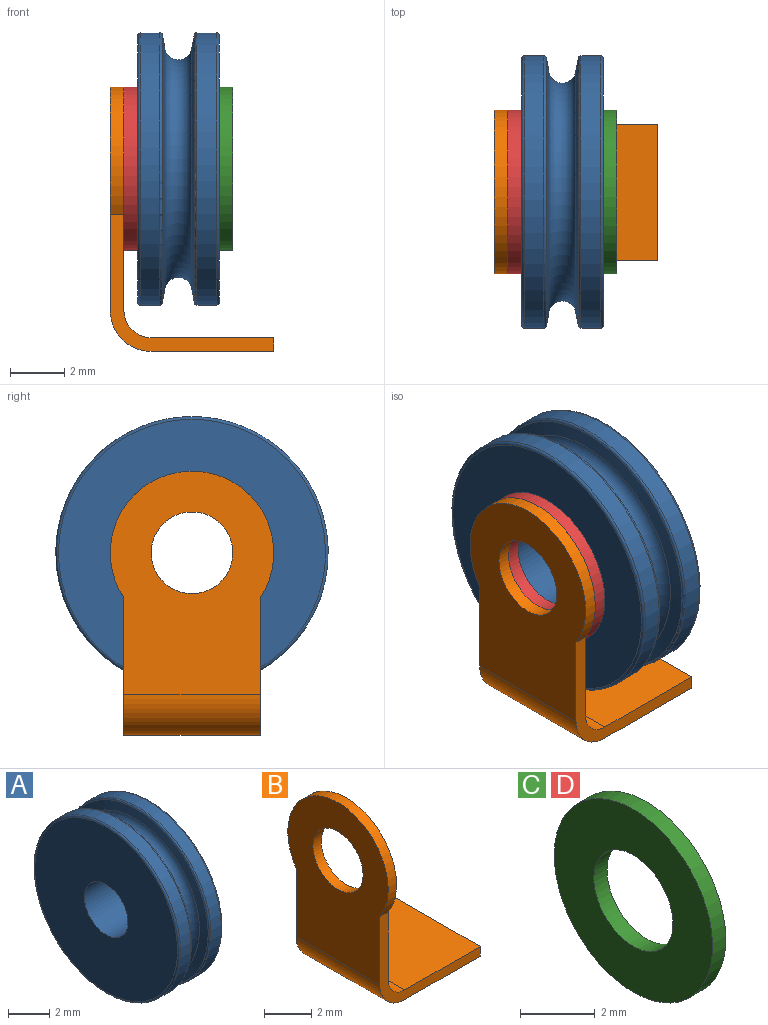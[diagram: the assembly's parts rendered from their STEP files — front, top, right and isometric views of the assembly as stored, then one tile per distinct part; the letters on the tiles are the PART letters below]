
ASSEMBLY  parts=4 mates=3
PART A: 12 faces, bbox 3x10.8x10.8 mm
  f0: cylinder r=1.5mm len=3mm, axis (-1,0,0), area 28.3mm2, adj f1,f2
  f1: plane 9.8x9.8mm, normal (1,0,0), area 68.4mm2, adj f0,f10
  f2: plane 9.8x9.8mm, normal (-1,0,0), area 68.4mm2, adj f0,f9
  f3: torus R=4.5mm, axis (-1,0,0), area 36.2mm2, adj f5,f6
  f4: cylinder r=5mm len=10mm, axis (-1,0,0), area 22.5mm2, adj f10,f11
  f5: cone r=5mm half-angle=79.6deg, axis (1,0,0), area 15.1mm2, adj f3,f11
  f6: cone r=5mm half-angle=79.6deg, axis (-1,0,0), area 15.1mm2, adj f3,f8
  f7: cylinder r=5mm len=10mm, axis (-1,0,0), area 22.5mm2, adj f8,f9
  f8: torus R=4.9mm, axis (1,0,0), area 4.3mm2, adj f6,f7
  f9: torus R=4.9mm, axis (1,0,0), area 4.9mm2, adj f2,f7
  f10: torus R=4.9mm, axis (1,0,0), area 4.9mm2, adj f1,f4
  f11: torus R=4.9mm, axis (1,0,0), area 4.3mm2, adj f4,f5
PART B: 11 faces, bbox 6x6x9.7 mm
  f0: plane 5x4.5mm, normal (0,0,-1), area 22.5mm2, adj f1,f2,f4,f10
  f1: plane 6x5.04mm, normal (0,-1,0), area 5mm2, adj f0,f3,f4,f5,f6,f8,f9,f10
  f2: plane 6x5.04mm, normal (0,1,0), area 5mm2, adj f0,f3,f4,f5,f6,f8,f9,f10
  f3: plane 8.2x6mm, normal (-1,0,0), area 34.2mm2, adj f1,f2,f6,f7,f10
  f4: plane 5x0.5mm, normal (1,0,0), area 2.5mm2, adj f0,f1,f2,f5
  f5: plane 5x4.5mm, normal (0,0,1), area 22.5mm2, adj f1,f2,f4,f9
  f6: cylinder r=3mm len=6mm, axis (1,0,0), area 6.5mm2, adj f1,f2,f3,f8
  f7: cylinder r=1.5mm len=3mm, axis (1,0,0), area 4.7mm2, adj f3,f8
  f8: plane 8.2x6mm, normal (1,0,0), area 34.2mm2, adj f1,f2,f6,f7,f9
  f9: cylinder r=1mm len=5mm, axis (0,1,0), area 7.9mm2, adj f1,f2,f5,f8
  f10: cylinder r=1.5mm len=5mm, axis (0,-1,0), area 11.8mm2, adj f0,f1,f2,f3
PART C: 4 faces, bbox 0.5x6x6 mm
  f0: cylinder r=1.5mm len=3mm, axis (-1,0,0), area 4.7mm2, adj f2,f3
  f1: cylinder r=3mm len=6mm, axis (-1,0,0), area 9.4mm2, adj f2,f3
  f2: plane 6x6mm, normal (1,0,0), area 21.2mm2, adj f0,f1
  f3: plane 6x6mm, normal (-1,0,0), area 21.2mm2, adj f0,f1
PART D: same geometry as C
PLACE A t=(-2,20,-4.6)mm
PLACE B t=(-2,20,-4.6)mm
PLACE C t=(-2,20,-4.6)mm
PLACE D t=(-5.5,20,-4.6)mm
MATE fastened D.f0 <-> C.f0  axis (1,0,0) through (-3.5,0,0)mm
MATE fastened B.f6 <-> D.f0  axis (1,0,0) through (-4,0,0)mm
MATE revolute A.f0 <-> C.f0  axis (-1,0,0) through (-0.5,0,0)mm
